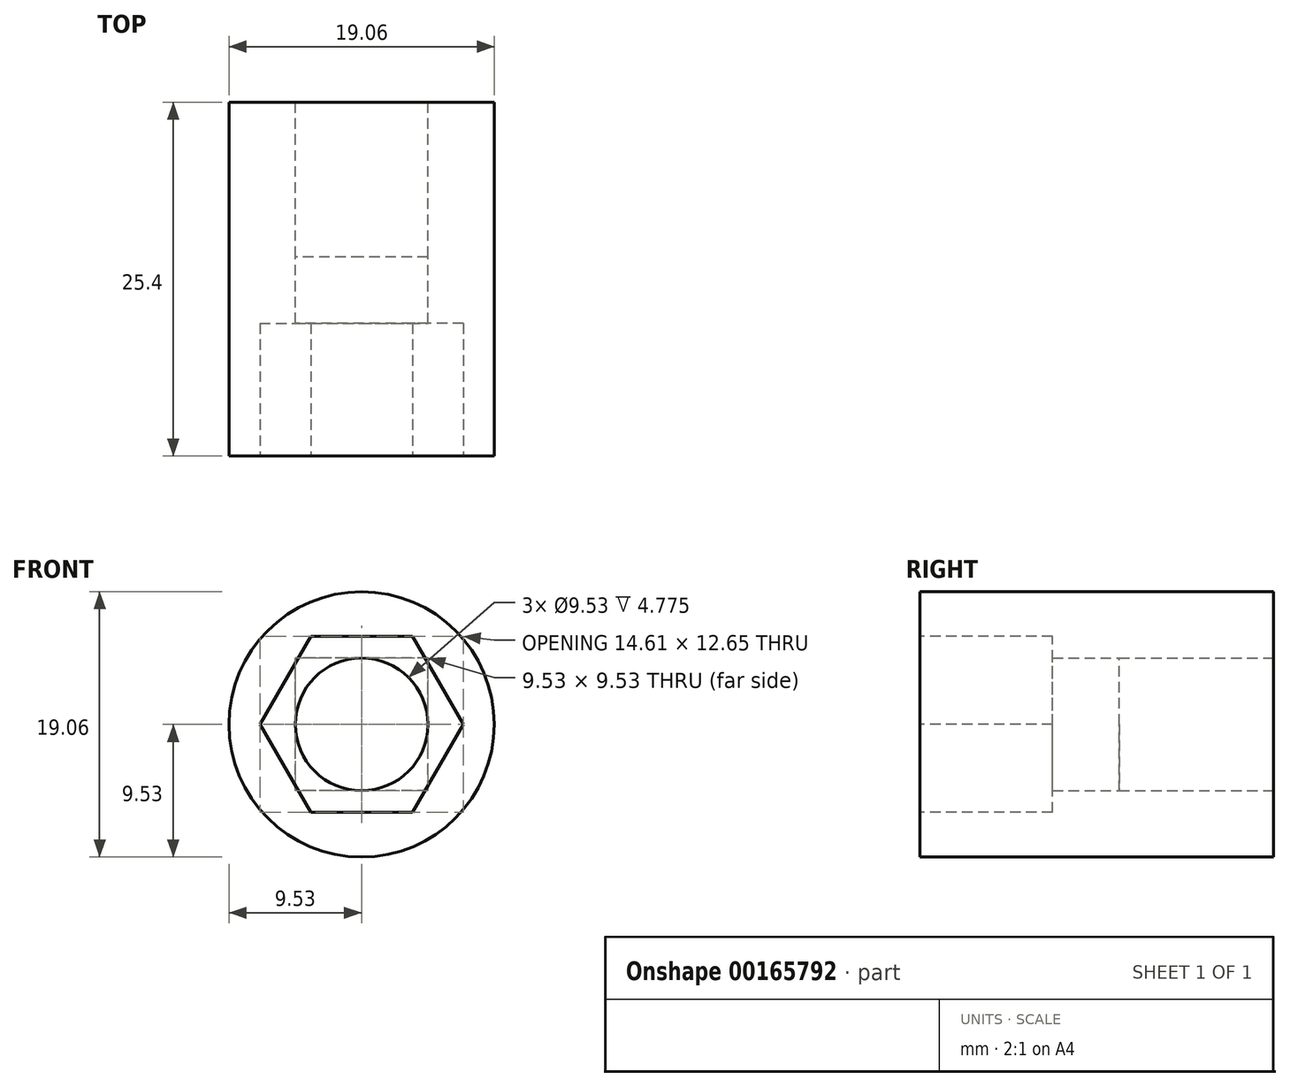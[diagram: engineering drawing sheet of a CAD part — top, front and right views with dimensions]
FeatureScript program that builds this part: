
annotation { "Feature Type Name" : "Feature", "Feature Type Description" : "" }
export const myFeature = defineFeature(function(context is Context, id is Id, definition is map)
    precondition{}
    {
        {
            var Q0;
            Q0=qCreatedBy(makeId("Front.planeOp"),FACE);
            var sketch = newSketch(context, id + "F0", { "sketchPlane" : qUnion([Q0])});
            skCircle(sketch, "E0", {"center": v(0, 0) * mm, "radius": 9.53 * mm});
            skSolve(sketch);
        }
        {
            var Q0;
            Q0 = qSketchRegion(id + "F0", true);
            extrude(context, id + "F1", {"entities" : qUnion([Q0]), "depth" : 25.4 * mm});
        }
        {
            var Q0;
            Q0=qCreatedBy(makeId("Front.planeOp"),FACE);
            var sketch = newSketch(context, id + "F2", { "sketchPlane" : qUnion([Q0])});
            skLineSegment(sketch, "E1.bottom", {"start": v(4.76, -4.76) * mm, "end": v(-4.76, -4.76) * mm});
            skLineSegment(sketch, "E1.top", {"start": v(4.76, 4.76) * mm, "end": v(-4.76, 4.76) * mm});
            skLineSegment(sketch, "E1.left", {"start": v(4.76, -4.76) * mm, "end": v(4.76, 4.76) * mm});
            skLineSegment(sketch, "E1.right", {"start": v(-4.76, -4.76) * mm, "end": v(-4.76, 4.76) * mm});
            skPoint(sketch, "E1.middle", {"position": v(0, 0) * mm});
            skCircle(sketch, "E2", {"center": v(0, 0) * mm, "radius": 4.76 * mm});
            skSolve(sketch);
        }
        {
            var Q0;
            {var subQ0=sQuery(id+"F2.wireOp",EDGE,"E2");var subQ1=makeQuery(id+"F2.imprint","INTERSECT",VERTEX,{"derivedFrom":[sQuery(id+"F2.wireOp",EDGE,"E1.top"),subQ0]});Q0=makeQuery(id+"F2.imprint","IMPRINT",FACE,{"disambiguationData":[TD([[makeQuery(id+"F2.imprint","IMPRINT",EDGE,{"disambiguationData":[TD([[subQ1,1.0]])],"derivedFrom":subQ0}),1.0]])]});}
            var Q1;
            Q1=sQuery(id+"F2.wireOp",EDGE,"E2");
            extrude(context, id + "F3", {"entities" : qUnion([Q0]), "operationType" : NewBodyOperationType.REMOVE, "surfaceEntities" : qUnion([Q1]), "endBound" : BoundingType.THROUGH_ALL, "depth" : 25.4 * mm});
        }
        {
            var Q0;
            Q0 = qSketchRegion(id + "F2", true);
            var Q1;
            Q1=sQuery(id+"F2.wireOp",EDGE,"E1.top");
            var Q2;
            Q2=sQuery(id+"F2.wireOp",EDGE,"E1.left");
            var Q3;
            Q3=sQuery(id+"F2.wireOp",EDGE,"E1.bottom");
            var Q4;
            Q4=sQuery(id+"F2.wireOp",EDGE,"E1.right");
            extrude(context, id + "F4", {"entities" : qUnion([Q0]), "operationType" : NewBodyOperationType.REMOVE, "surfaceEntities" : qUnion([Q1, Q2, Q3, Q4]), "depth" : 11.1 * mm});
        }
        {
            var Q0;
            Q0=makeQuery(id+"F1.opExtrude","CAP_FACE",FACE,{"disambiguationData":[OSD([sQuery(id+"F0.wireOp",EDGE,"E0")])],"isStart":false});
            var sketch = newSketch(context, id + "F5", { "sketchPlane" : qUnion([Q0])});
            skCircle(sketch, "E3.cCircle", {"center": v(0, 0) * mm, "radius": 6.32 * mm, "construction": true});
            skLineSegment(sketch, "E3.0", {"start": v(-3.65, 6.32) * mm, "end": v(3.65, 6.32) * mm});
            skLineSegment(sketch, "E3.1", {"start": v(3.65, 6.32) * mm, "end": v(7.3, 0) * mm});
            skLineSegment(sketch, "E3.2", {"start": v(7.3, 0) * mm, "end": v(3.65, -6.32) * mm});
            skLineSegment(sketch, "E3.3", {"start": v(3.65, -6.32) * mm, "end": v(-3.65, -6.32) * mm});
            skLineSegment(sketch, "E3.4", {"start": v(-3.65, -6.32) * mm, "end": v(-7.3, 0) * mm});
            skLineSegment(sketch, "E3.5", {"start": v(-7.3, 0) * mm, "end": v(-3.65, 6.32) * mm});
            skPoint(sketch, "E3.0.midPoint", {"position": v(0, 6.32) * mm});
            skSolve(sketch);
        }
        {
            var Q0;
            Q0 = qSketchRegion(id + "F5", true);
            extrude(context, id + "F6", {"entities" : qUnion([Q0]), "operationType" : NewBodyOperationType.REMOVE, "oppositeDirection" : true, "depth" : 9.52 * mm});
        }
    });
